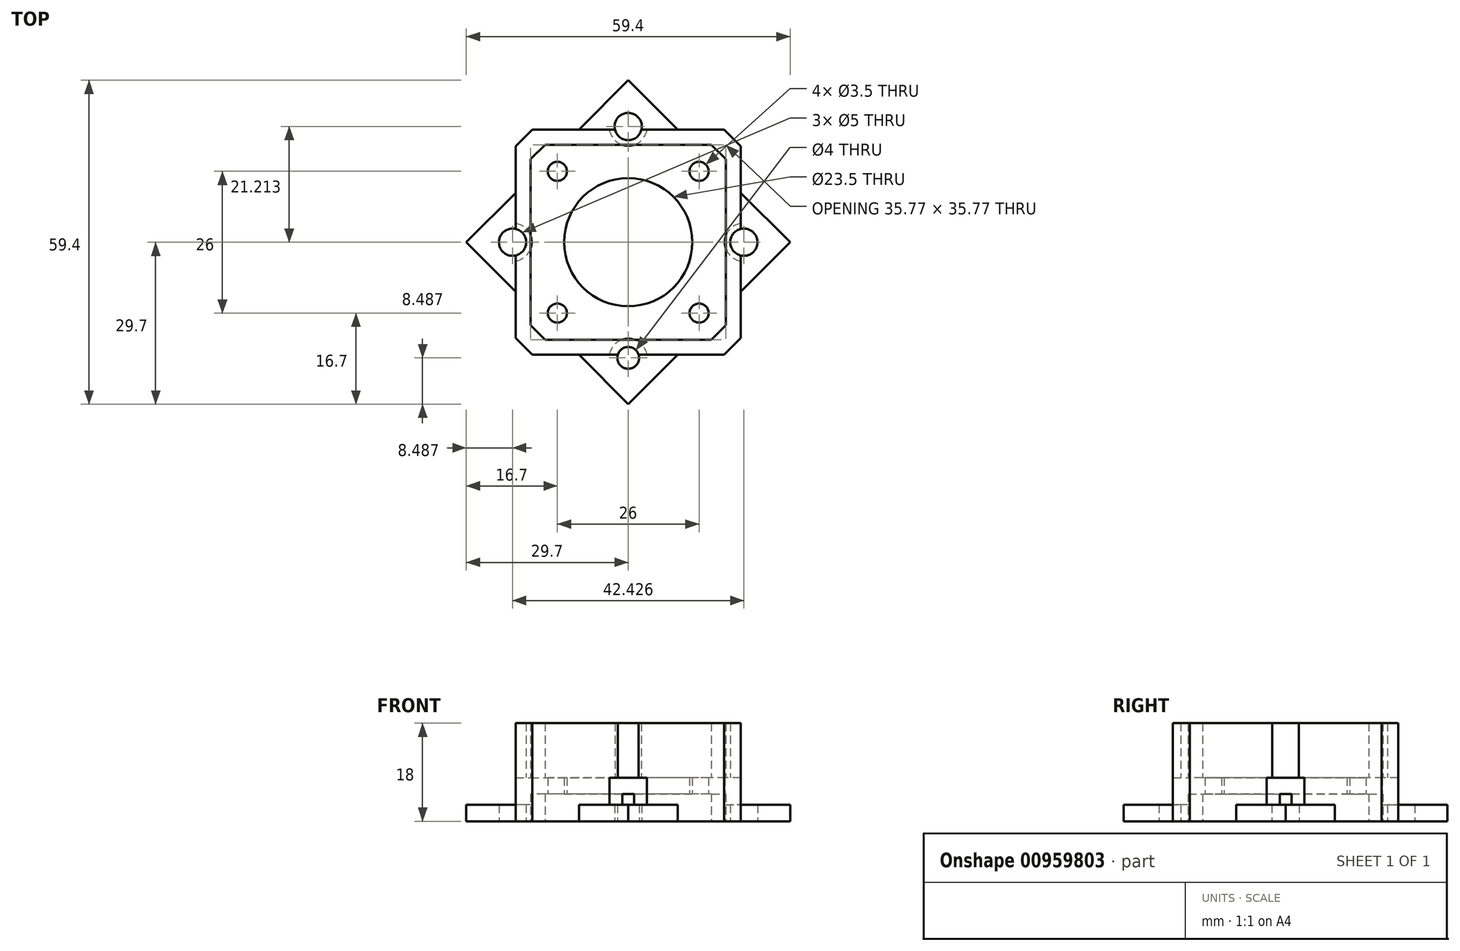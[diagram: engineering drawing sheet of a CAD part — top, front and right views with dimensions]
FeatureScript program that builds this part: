
annotation { "Feature Type Name" : "Feature", "Feature Type Description" : "" }
export const myFeature = defineFeature(function(context is Context, id is Id, definition is map)
    precondition{}
    {
        {
            var Q0;
            Q0=qCreatedBy(makeId("Top.planeOp"),FACE);
            var sketch = newSketch(context, id + "F0", { "sketchPlane" : qUnion([Q0])});
            skLineSegment(sketch, "E0", {"start": v(0, 0) * mm, "end": v(-17.6, 15) * mm});
            skLineSegment(sketch, "E1", {"start": v(0, 0) * mm, "end": v(-15, 17.6) * mm});
            skLineSegment(sketch, "E2", {"start": v(0, 0) * mm, "end": v(-17.6, -15) * mm});
            skLineSegment(sketch, "E3", {"start": v(0, 0) * mm, "end": v(-15, -17.6) * mm});
            skLineSegment(sketch, "E4", {"start": v(0, 0) * mm, "end": v(15, 17.6) * mm});
            skLineSegment(sketch, "E5", {"start": v(0, 0) * mm, "end": v(17.6, 15) * mm});
            skLineSegment(sketch, "E6", {"start": v(0, 0) * mm, "end": v(15, -17.6) * mm});
            skLineSegment(sketch, "E7", {"start": v(0, 0) * mm, "end": v(17.6, -15) * mm});
            skLineSegment(sketch, "E8", {"start": v(0, 0) * mm, "end": v(15.24, 17.89) * mm});
            skLineSegment(sketch, "E9", {"start": v(0, 0) * mm, "end": v(17.89, 15.24) * mm});
            skLineSegment(sketch, "E10", {"start": v(0, 0) * mm, "end": v(17.89, -15.24) * mm});
            skLineSegment(sketch, "E11", {"start": v(0, 0) * mm, "end": v(15.24, -17.89) * mm});
            skLineSegment(sketch, "E12", {"start": v(0, 0) * mm, "end": v(-15.24, -17.89) * mm});
            skLineSegment(sketch, "E13", {"start": v(0, 0) * mm, "end": v(-17.89, -15.24) * mm});
            skLineSegment(sketch, "E14", {"start": v(0, 0) * mm, "end": v(-15.24, 17.89) * mm});
            skLineSegment(sketch, "E15", {"start": v(0, 0) * mm, "end": v(-17.89, 15.24) * mm});
            skLineSegment(sketch, "E16", {"start": v(0, 0) * mm, "end": v(17.6, 20.65) * mm});
            skLineSegment(sketch, "E17", {"start": v(17.6, 20.65) * mm, "end": v(0, 0) * mm});
            skLineSegment(sketch, "E18", {"start": v(0, 0) * mm, "end": v(20.65, 17.6) * mm});
            skLineSegment(sketch, "E19", {"start": v(0, 0) * mm, "end": v(20.65, -17.6) * mm});
            skLineSegment(sketch, "E20", {"start": v(0, 0) * mm, "end": v(17.6, -20.65) * mm});
            skLineSegment(sketch, "E21", {"start": v(0, 0) * mm, "end": v(-17.6, -20.65) * mm});
            skLineSegment(sketch, "E22", {"start": v(0, 0) * mm, "end": v(-20.65, -17.6) * mm});
            skLineSegment(sketch, "E23", {"start": v(0, 0) * mm, "end": v(-20.65, 17.6) * mm});
            skLineSegment(sketch, "E24", {"start": v(0, 0) * mm, "end": v(-17.6, 20.65) * mm});
            skSolve(sketch);
        }
        {
            var Q0;
            Q0=qCreatedBy(makeId("Top.planeOp"),FACE);
            var sketch = newSketch(context, id + "F1", { "sketchPlane" : qUnion([Q0])});
            skLineSegment(sketch, "E25", {"start": v(-17.89, -15.24) * mm, "end": v(-17.89, 15.24) * mm});
            skLineSegment(sketch, "E26", {"start": v(-17.89, 15.24) * mm, "end": v(-15.24, 17.89) * mm});
            skLineSegment(sketch, "E27", {"start": v(-15.24, 17.89) * mm, "end": v(15.24, 17.89) * mm});
            skLineSegment(sketch, "E28", {"start": v(15.24, 17.89) * mm, "end": v(17.89, 15.24) * mm});
            skLineSegment(sketch, "E29", {"start": v(17.89, 15.24) * mm, "end": v(17.89, -15.24) * mm});
            skLineSegment(sketch, "E30", {"start": v(17.89, -15.24) * mm, "end": v(15.24, -17.89) * mm});
            skLineSegment(sketch, "E31", {"start": v(15.24, -17.89) * mm, "end": v(-15.24, -17.89) * mm});
            skLineSegment(sketch, "E32", {"start": v(-15.24, -17.89) * mm, "end": v(-17.89, -15.24) * mm});
            skLineSegment(sketch, "E33", {"start": v(-20.65, 17.6) * mm, "end": v(-20.65, -17.6) * mm});
            skLineSegment(sketch, "E34", {"start": v(-20.65, -17.6) * mm, "end": v(-17.6, -20.65) * mm});
            skLineSegment(sketch, "E35", {"start": v(-17.6, -20.65) * mm, "end": v(17.6, -20.65) * mm});
            skLineSegment(sketch, "E36", {"start": v(17.6, -20.65) * mm, "end": v(20.65, -17.6) * mm});
            skLineSegment(sketch, "E37", {"start": v(20.65, -17.6) * mm, "end": v(20.65, 17.6) * mm});
            skLineSegment(sketch, "E38", {"start": v(20.65, 17.6) * mm, "end": v(17.6, 20.65) * mm});
            skLineSegment(sketch, "E39", {"start": v(17.6, 20.65) * mm, "end": v(-17.6, 20.65) * mm});
            skLineSegment(sketch, "E40", {"start": v(-17.6, 20.65) * mm, "end": v(-20.65, 17.6) * mm});
            skSolve(sketch);
        }
        {
            var Q0;
            Q0=qCreatedBy(makeId("Top.planeOp"),FACE);
            var sketch = newSketch(context, id + "F2", { "sketchPlane" : qUnion([Q0])});
            skCircle(sketch, "E41", {"center": v(0, 0) * mm, "radius": 11.75 * mm});
            skCircle(sketch, "E42", {"center": v(13, 13) * mm, "radius": 1.75 * mm});
            skCircle(sketch, "E43.MirrorC", {"center": v(-13, -13) * mm, "radius": 1.75 * mm});
            skCircle(sketch, "E44.MirrorC", {"center": v(13, -13) * mm, "radius": 1.75 * mm});
            skLineSegment(sketch, "E45", {"start": v(-17.89, 15.24) * mm, "end": v(-15.24, 17.89) * mm});
            skLineSegment(sketch, "E46", {"start": v(-15.24, 17.89) * mm, "end": v(15.24, 17.89) * mm});
            skLineSegment(sketch, "E47", {"start": v(15.24, 17.89) * mm, "end": v(17.89, 15.24) * mm});
            skLineSegment(sketch, "E48", {"start": v(17.89, 15.24) * mm, "end": v(17.89, -15.24) * mm});
            skLineSegment(sketch, "E49", {"start": v(17.89, -15.24) * mm, "end": v(15.24, -17.89) * mm});
            skLineSegment(sketch, "E50", {"start": v(15.24, -17.89) * mm, "end": v(-15.24, -17.89) * mm});
            skLineSegment(sketch, "E51", {"start": v(-15.24, -17.89) * mm, "end": v(-17.89, -15.24) * mm});
            skLineSegment(sketch, "E52", {"start": v(-17.89, -15.24) * mm, "end": v(-17.89, 15.24) * mm});
            skCircle(sketch, "E53.MirrorC", {"center": v(-13, 13) * mm, "radius": 1.75 * mm});
            skSolve(sketch);
        }
        {
            var Q0;
            Q0=qCreatedBy(makeId("Top.planeOp"),FACE);
            var sketch = newSketch(context, id + "F3", { "sketchPlane" : qUnion([Q0])});
            skLineSegment(sketch, "E54.bottom", {"start": v(0, -29.7) * mm, "end": v(-29.7, 0) * mm});
            skLineSegment(sketch, "E54.top", {"start": v(29.7, 0) * mm, "end": v(0, 29.7) * mm});
            skLineSegment(sketch, "E54.left", {"start": v(0, -29.7) * mm, "end": v(29.7, 0) * mm});
            skLineSegment(sketch, "E54.right", {"start": v(-29.7, 0) * mm, "end": v(0, 29.7) * mm});
            skPoint(sketch, "E54.middle", {"position": v(0, 0) * mm});
            skCircle(sketch, "E55", {"center": v(0, 0) * mm, "radius": 11.75 * mm});
            skCircle(sketch, "E56", {"center": v(0, 21.21) * mm, "radius": 2.5 * mm});
            skCircle(sketch, "E57", {"center": v(21.21, 0) * mm, "radius": 2.5 * mm});
            skCircle(sketch, "E58", {"center": v(-21.21, 0) * mm, "radius": 2.5 * mm});
            skCircle(sketch, "E59", {"center": v(0, -21.21) * mm, "radius": 2 * mm});
            skLineSegment(sketch, "E60.bottom", {"start": v(0, 21.21) * mm, "end": v(21.21, 0) * mm, "construction": true});
            skLineSegment(sketch, "E60.top", {"start": v(-21.21, 0) * mm, "end": v(0, -21.21) * mm, "construction": true});
            skLineSegment(sketch, "E60.left", {"start": v(0, 21.21) * mm, "end": v(-21.21, 0) * mm, "construction": true});
            skLineSegment(sketch, "E60.right", {"start": v(21.21, 0) * mm, "end": v(0, -21.21) * mm, "construction": true});
            skCircle(sketch, "E61", {"center": v(-13, 13) * mm, "radius": 1.75 * mm});
            skCircle(sketch, "E62", {"center": v(-13, -13) * mm, "radius": 1.75 * mm});
            skCircle(sketch, "E63", {"center": v(13, -13) * mm, "radius": 1.75 * mm});
            skCircle(sketch, "E64", {"center": v(13, 13) * mm, "radius": 1.75 * mm});
            skSolve(sketch);
        }
        {
            var Q0;
            Q0=makeQuery(id+"F1.imprint","IMPRINT",FACE,{"disambiguationData":[TD([[makeQuery(id+"F1.imprint","IMPRINT",EDGE,{"derivedFrom":sQuery(id+"F1.wireOp",EDGE,"E25")}),1.0]])]});
            extrude(context, id + "F4", {"entities" : qUnion([Q0]), "depth" : 18 * mm, "offsetDistance" : 25 * mm});
        }
        {
            var Q0;
            Q0=makeQuery(id+"F2.imprint","IMPRINT",FACE,{"disambiguationData":[TD([[makeQuery(id+"F2.imprint","IMPRINT",EDGE,{"derivedFrom":sQuery(id+"F2.wireOp",EDGE,"E41")}),-1.0]])]});
            extrude(context, id + "F5", {"entities" : qUnion([Q0]), "operationType" : NewBodyOperationType.ADD, "depth" : 8 * mm, "offsetDistance" : 25 * mm});
        }
        {
            var Q0;
            Q0=makeQuery(id+"F3.imprint","IMPRINT",FACE,{"disambiguationData":[TD([[makeQuery(id+"F3.imprint","IMPRINT",EDGE,{"derivedFrom":sQuery(id+"F3.wireOp",EDGE,"E54.bottom")}),-1.0]])]});
            extrude(context, id + "F6", {"entities" : qUnion([Q0]), "operationType" : NewBodyOperationType.ADD, "depth" : 3 * mm, "offsetDistance" : 25 * mm});
        }
        {
            var Q0;
            Q0=makeQuery(id+"F3.imprint","IMPRINT",FACE,{"disambiguationData":[TD([[makeQuery(id+"F3.imprint","IMPRINT",EDGE,{"derivedFrom":sQuery(id+"F3.wireOp",EDGE,"E57")}),1.0]])]});
            var Q1;
            Q1=makeQuery(id+"F3.imprint","IMPRINT",FACE,{"disambiguationData":[TD([[makeQuery(id+"F3.imprint","IMPRINT",EDGE,{"derivedFrom":sQuery(id+"F3.wireOp",EDGE,"E56")}),1.0]])]});
            var Q2;
            Q2=makeQuery(id+"F3.imprint","IMPRINT",FACE,{"disambiguationData":[TD([[makeQuery(id+"F3.imprint","IMPRINT",EDGE,{"derivedFrom":sQuery(id+"F3.wireOp",EDGE,"E59")}),1.0]])]});
            var Q3;
            Q3=makeQuery(id+"F3.imprint","IMPRINT",FACE,{"disambiguationData":[TD([[makeQuery(id+"F3.imprint","IMPRINT",EDGE,{"derivedFrom":sQuery(id+"F3.wireOp",EDGE,"E58")}),1.0]])]});
            extrude(context, id + "F7", {"entities" : qUnion([Q0, Q1, Q2, Q3]), "operationType" : NewBodyOperationType.REMOVE, "oppositeDirection" : true, "depth" : -18 * mm, "offsetDistance" : 25 * mm});
        }
        {
            var Q0;
            Q0=makeQuery(id+"F6.boolean.opBoolean","MERGE",FACE,{"derivedFrom":[makeQuery(id+"F5.boolean.opBoolean","MERGE",FACE,{"derivedFrom":[makeQuery(id+"F4.opExtrude","CAP_FACE",FACE,{"disambiguationData":[OSD([sQuery(id+"F1.wireOp",EDGE,"E25"),sQuery(id+"F1.wireOp",EDGE,"E26"),sQuery(id+"F1.wireOp",EDGE,"E27"),sQuery(id+"F1.wireOp",EDGE,"E28"),sQuery(id+"F1.wireOp",EDGE,"E29"),sQuery(id+"F1.wireOp",EDGE,"E30"),sQuery(id+"F1.wireOp",EDGE,"E31"),sQuery(id+"F1.wireOp",EDGE,"E32"),sQuery(id+"F1.wireOp",EDGE,"E33"),sQuery(id+"F1.wireOp",EDGE,"E34"),sQuery(id+"F1.wireOp",EDGE,"E35"),sQuery(id+"F1.wireOp",EDGE,"E36"),sQuery(id+"F1.wireOp",EDGE,"E37"),sQuery(id+"F1.wireOp",EDGE,"E38"),sQuery(id+"F1.wireOp",EDGE,"E39"),sQuery(id+"F1.wireOp",EDGE,"E40")])],"isStart":true}),makeQuery(id+"F5.opExtrude","CAP_FACE",FACE,{"disambiguationData":[OSD([sQuery(id+"F2.wireOp",EDGE,"E41"),sQuery(id+"F2.wireOp",EDGE,"E42"),sQuery(id+"F2.wireOp",EDGE,"E43.MirrorC"),sQuery(id+"F2.wireOp",EDGE,"E44.MirrorC"),sQuery(id+"F2.wireOp",EDGE,"E45"),sQuery(id+"F2.wireOp",EDGE,"E46"),sQuery(id+"F2.wireOp",EDGE,"E47"),sQuery(id+"F2.wireOp",EDGE,"E48"),sQuery(id+"F2.wireOp",EDGE,"E49"),sQuery(id+"F2.wireOp",EDGE,"E50"),sQuery(id+"F2.wireOp",EDGE,"E51"),sQuery(id+"F2.wireOp",EDGE,"E52"),sQuery(id+"F2.wireOp",EDGE,"E53.MirrorC")])],"isStart":true})]}),makeQuery(id+"F6.opExtrude","CAP_FACE",FACE,{"disambiguationData":[OSD([sQuery(id+"F3.wireOp",EDGE,"E54.bottom"),sQuery(id+"F3.wireOp",EDGE,"E54.top"),sQuery(id+"F3.wireOp",EDGE,"E54.left"),sQuery(id+"F3.wireOp",EDGE,"E54.right"),sQuery(id+"F3.wireOp",EDGE,"E55"),sQuery(id+"F3.wireOp",EDGE,"E56"),sQuery(id+"F3.wireOp",EDGE,"E57"),sQuery(id+"F3.wireOp",EDGE,"E58"),sQuery(id+"F3.wireOp",EDGE,"E59"),sQuery(id+"F3.wireOp",EDGE,"E61"),sQuery(id+"F3.wireOp",EDGE,"E62"),sQuery(id+"F3.wireOp",EDGE,"E63"),sQuery(id+"F3.wireOp",EDGE,"E64")])],"isStart":true})]});
            var sketch = newSketch(context, id + "F8", { "sketchPlane" : qUnion([Q0])});
            skCircle(sketch, "E65", {"center": v(13, 13) * mm, "radius": 4.5 * mm});
            skCircle(sketch, "E66", {"center": v(-13, -13) * mm, "radius": 4.5 * mm});
            skCircle(sketch, "E67", {"center": v(13, -13) * mm, "radius": 4.5 * mm});
            skCircle(sketch, "E68", {"center": v(-13, 13) * mm, "radius": 4.5 * mm});
            skSolve(sketch);
        }
        {
            var Q0;
            Q0=makeQuery(id+"F8.imprint","IMPRINT",FACE,{"disambiguationData":[TD([[makeQuery(id+"F8.imprint","IMPRINT",EDGE,{"derivedFrom":sQuery(id+"F8.wireOp",EDGE,"E66")}),1.0]])]});
            var Q1;
            Q1=makeQuery(id+"F2.imprint","IMPRINT",FACE,{"disambiguationData":[TD([[makeQuery(id+"F2.imprint","IMPRINT",EDGE,{"derivedFrom":sQuery(id+"F2.wireOp",EDGE,"E53.MirrorC")}),-1.0]])]});
            extrude(context, id + "F9", {"entities" : qUnion([Q0, Q1]), "operationType" : NewBodyOperationType.REMOVE, "oppositeDirection" : true, "depth" : 5 * mm, "offsetDistance" : 25 * mm});
        }
        {
            var Q0;
            Q0=makeQuery(id+"F8.imprint","IMPRINT",FACE,{"disambiguationData":[TD([[makeQuery(id+"F8.imprint","IMPRINT",EDGE,{"derivedFrom":sQuery(id+"F8.wireOp",EDGE,"E65")}),1.0]])]});
            var Q1;
            Q1=makeQuery(id+"F2.imprint","IMPRINT",FACE,{"disambiguationData":[TD([[makeQuery(id+"F2.imprint","IMPRINT",EDGE,{"derivedFrom":sQuery(id+"F2.wireOp",EDGE,"E44.MirrorC")}),-1.0]])]});
            extrude(context, id + "F10", {"entities" : qUnion([Q0, Q1]), "operationType" : NewBodyOperationType.REMOVE, "oppositeDirection" : true, "depth" : 5 * mm, "offsetDistance" : 25 * mm});
        }
        {
            var Q0;
            {var subQ0=sQuery(id+"F3.wireOp",EDGE,"E54.top");var subQ1=sQuery(id+"F3.wireOp",EDGE,"E54.right");var subQ2=sQuery(id+"F3.wireOp",EDGE,"E56");Q0=makeQuery(id+"F6.boolean.opBoolean","SPLIT",FACE,{"disambiguationData":[TD([makeQuery(id+"F4.opExtrude","SWEPT_FACE",FACE,{"disambiguationData":[OSD([sQuery(id+"F1.wireOp",EDGE,"E39")])]})])],"derivedFrom":makeQuery(id+"F6.opExtrude","CAP_FACE",FACE,{"disambiguationData":[OSD([sQuery(id+"F3.wireOp",EDGE,"E54.bottom"),subQ0,sQuery(id+"F3.wireOp",EDGE,"E54.left"),subQ1,sQuery(id+"F3.wireOp",EDGE,"E55"),subQ2,sQuery(id+"F3.wireOp",EDGE,"E57"),sQuery(id+"F3.wireOp",EDGE,"E58"),sQuery(id+"F3.wireOp",EDGE,"E59"),sQuery(id+"F3.wireOp",EDGE,"E61"),sQuery(id+"F3.wireOp",EDGE,"E62"),sQuery(id+"F3.wireOp",EDGE,"E63"),sQuery(id+"F3.wireOp",EDGE,"E64")])],"isStart":false})});}
            var sketch = newSketch(context, id + "F11", { "sketchPlane" : qUnion([Q0])});
            skCircle(sketch, "E69", {"center": v(0, 21.21) * mm, "radius": 3.5 * mm});
            skCircle(sketch, "E70", {"center": v(0, -21.21) * mm, "radius": 3.5 * mm});
            skCircle(sketch, "E71", {"center": v(21.21, 0) * mm, "radius": 3.5 * mm});
            skCircle(sketch, "E72", {"center": v(-21.21, 0) * mm, "radius": 3.5 * mm});
            skSolve(sketch);
        }
        {
            var Q0;
            Q0=qSketchRegion(id+"F11",true);
            extrude(context, id + "F12", {"entities" : qUnion([Q0]), "operationType" : NewBodyOperationType.REMOVE, "oppositeDirection" : true, "depth" : -5 * mm, "offsetDistance" : 25 * mm});
        }
        {
            var Q0;
            Q0=makeQuery(id+"F8.imprint","IMPRINT",FACE,{"disambiguationData":[TD([[makeQuery(id+"F8.imprint","IMPRINT",EDGE,{"derivedFrom":sQuery(id+"F8.wireOp",EDGE,"E67")}),1.0]])]});
            extrude(context, id + "F13", {"entities" : qUnion([Q0]), "operationType" : NewBodyOperationType.REMOVE, "oppositeDirection" : true, "depth" : 5 * mm, "offsetDistance" : 25 * mm});
        }
        {
            var Q0;
            Q0=makeQuery(id+"F8.imprint","IMPRINT",FACE,{"disambiguationData":[TD([[makeQuery(id+"F8.imprint","IMPRINT",EDGE,{"derivedFrom":sQuery(id+"F8.wireOp",EDGE,"E68")}),1.0]])]});
            extrude(context, id + "F14", {"entities" : qUnion([Q0]), "operationType" : NewBodyOperationType.REMOVE, "oppositeDirection" : true, "depth" : 5 * mm, "offsetDistance" : 25 * mm});
        }
    });
